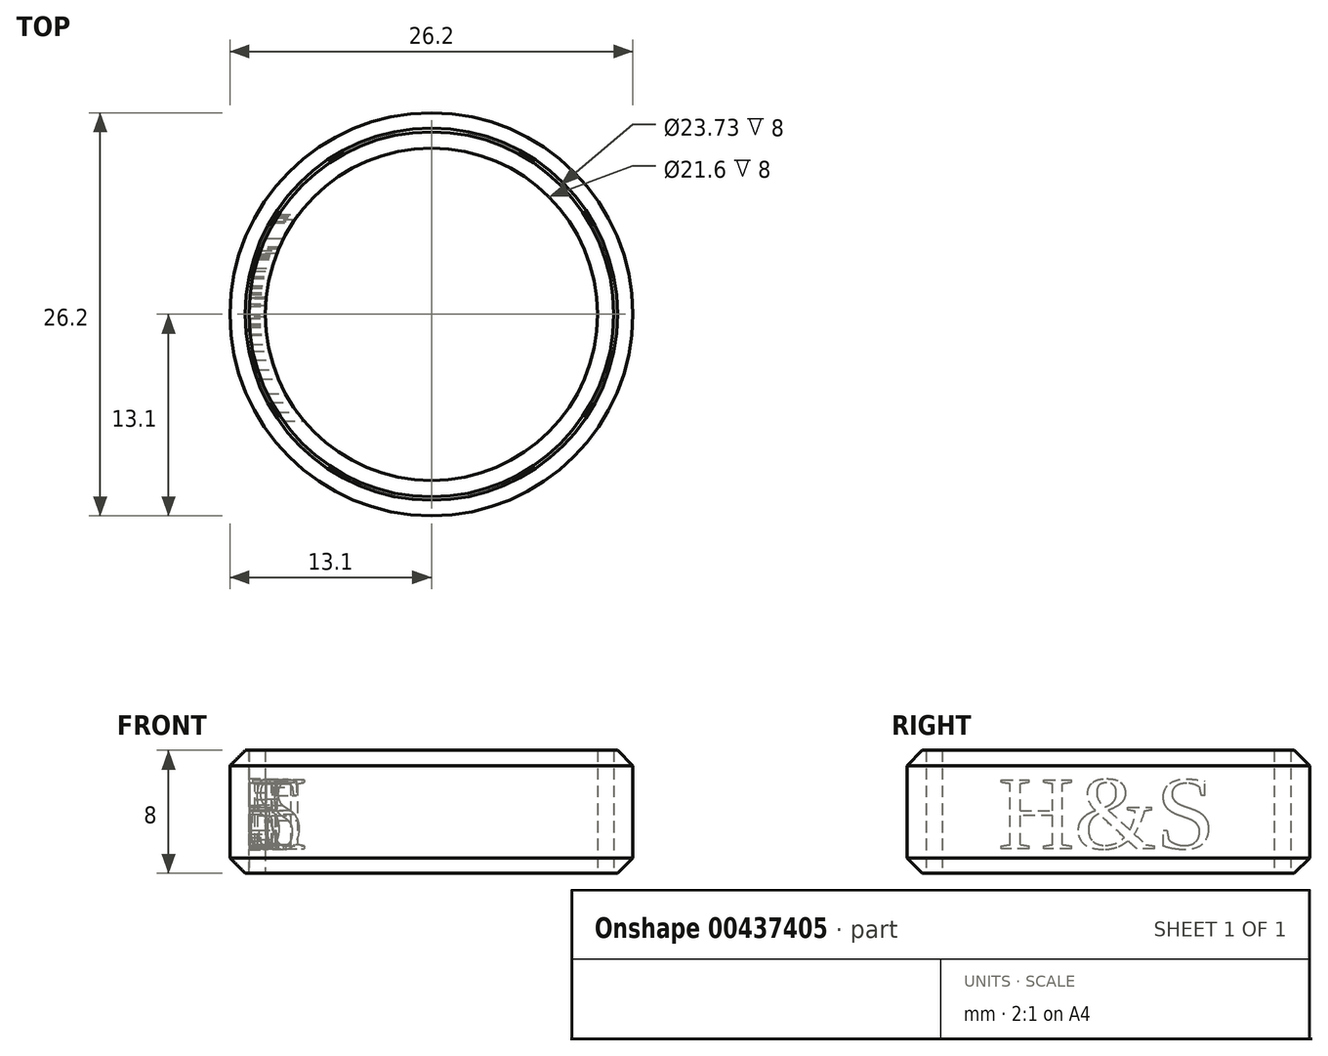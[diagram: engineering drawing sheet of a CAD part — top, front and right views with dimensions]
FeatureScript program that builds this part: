
annotation { "Feature Type Name" : "Feature", "Feature Type Description" : "" }
export const myFeature = defineFeature(function(context is Context, id is Id, definition is map)
    precondition{}
    {
        {
            var Q0;
            Q0=qCreatedBy(makeId("Top.planeOp"),FACE);
            var sketch = newSketch(context, id + "F0", { "sketchPlane" : qUnion([Q0])});
            skCircle(sketch, "E0", {"center": v(0, 0) * mm, "radius": 10.8 * mm});
            skCircle(sketch, "E1", {"center": v(0, 0) * mm, "radius": 13 * mm});
            skSolve(sketch);
        }
        {
            var Q0;
            Q0=makeQuery(id+"F0.imprint","IMPRINT",FACE,{"disambiguationData":[TD([[makeQuery(id+"F0.imprint","IMPRINT",EDGE,{"derivedFrom":sQuery(id+"F0.wireOp",EDGE,"E0")}),-1.0]])]});
            extrude(context, id + "F1", {"entities" : qUnion([Q0]), "depth" : 8 * mm});
        }
        {
            var Q0;
            Q0=qCreatedBy(makeId("Right.planeOp"),FACE);
            var sketch = newSketch(context, id + "F2", { "sketchPlane" : qUnion([Q0])});
            skText(sketch, "E2", { "text": "H&S", "fontName": "Tinos-Regular.ttf"});
            const initialGuessF2  = {"E2": [-0.00715, 0.0016, 1, 0, 0.00493]};
            skSetInitialGuess(sketch, initialGuessF2);
            skSolve(sketch);
        }
        {
            var Q0;
            Q0 = qSketchRegion(id + "F2", true);
            extrude(context, id + "F3", {"entities" : qUnion([Q0]), "operationType" : NewBodyOperationType.REMOVE, "endBound" : BoundingType.THROUGH_ALL, "oppositeDirection" : true, "depth" : 25 * mm});
        }
        {
            var Q0;
            Q0=makeQuery(id+"F1.opExtrude","CAP_FACE",FACE,{"disambiguationData":[OSD([sQuery(id+"F0.wireOp",EDGE,"E0"),sQuery(id+"F0.wireOp",EDGE,"E1")])],"isStart":false});
            var sketch = newSketch(context, id + "F4", { "sketchPlane" : qUnion([Q0])});
            skCircle(sketch, "E3", {"center": v(0, 0) * mm, "radius": 13 * mm});
            skCircle(sketch, "E4", {"center": v(0, 0) * mm, "radius": 11.87 * mm});
            skSolve(sketch);
        }
        {
            var Q0;
            Q0=makeQuery(id+"F4.imprint","IMPRINT",FACE,{"disambiguationData":[TD([[makeQuery(id+"F4.imprint","IMPRINT",EDGE,{"derivedFrom":sQuery(id+"F4.wireOp",EDGE,"E4")}),-1.0]])]});
            extrude(context, id + "F5", {"entities" : qUnion([Q0]), "operationType" : NewBodyOperationType.REMOVE, "oppositeDirection" : true, "depth" : 25 * mm});
        }
        {
            var Q0;
            Q0=makeQuery(id+"F1.opExtrude","CAP_FACE",FACE,{"disambiguationData":[OSD([sQuery(id+"F0.wireOp",EDGE,"E0"),sQuery(id+"F0.wireOp",EDGE,"E1")])],"isStart":true});
            var sketch = newSketch(context, id + "F6", { "sketchPlane" : qUnion([Q0])});
            skCircle(sketch, "E5", {"center": v(0, 0) * mm, "radius": 13.1 * mm});
            skCircle(sketch, "E6", {"center": v(0, 0) * mm, "radius": 11.63 * mm});
            skSolve(sketch);
        }
        {
            var Q0;
            Q0=makeQuery(id+"F6.imprint","IMPRINT",FACE,{"disambiguationData":[TD([[makeQuery(id+"F6.imprint","IMPRINT",EDGE,{"derivedFrom":sQuery(id+"F6.wireOp",EDGE,"E5")}),1.0]])]});
            extrude(context, id + "F7", {"entities" : qUnion([Q0]), "oppositeDirection" : true, "depth" : 8 * mm});
        }
        {
            var Q0;
            Q0=makeQuery(id+"F7.opExtrude","CAP_EDGE",EDGE,{"disambiguationData":[OSD([sQuery(id+"F6.wireOp",EDGE,"E5")])],"isStart":true});
            chamfer(context, id + "F8", {"entities" : qUnion([Q0]), "width" : 1 * mm, "tangentPropagation" : true});
        }
        {
            var Q0;
            Q0=makeQuery(id+"F7.opExtrude","CAP_EDGE",EDGE,{"disambiguationData":[OSD([sQuery(id+"F6.wireOp",EDGE,"E5")])],"isStart":false});
            chamfer(context, id + "F9", {"entities" : qUnion([Q0]), "width" : 1 * mm, "tangentPropagation" : true});
        }
    });
